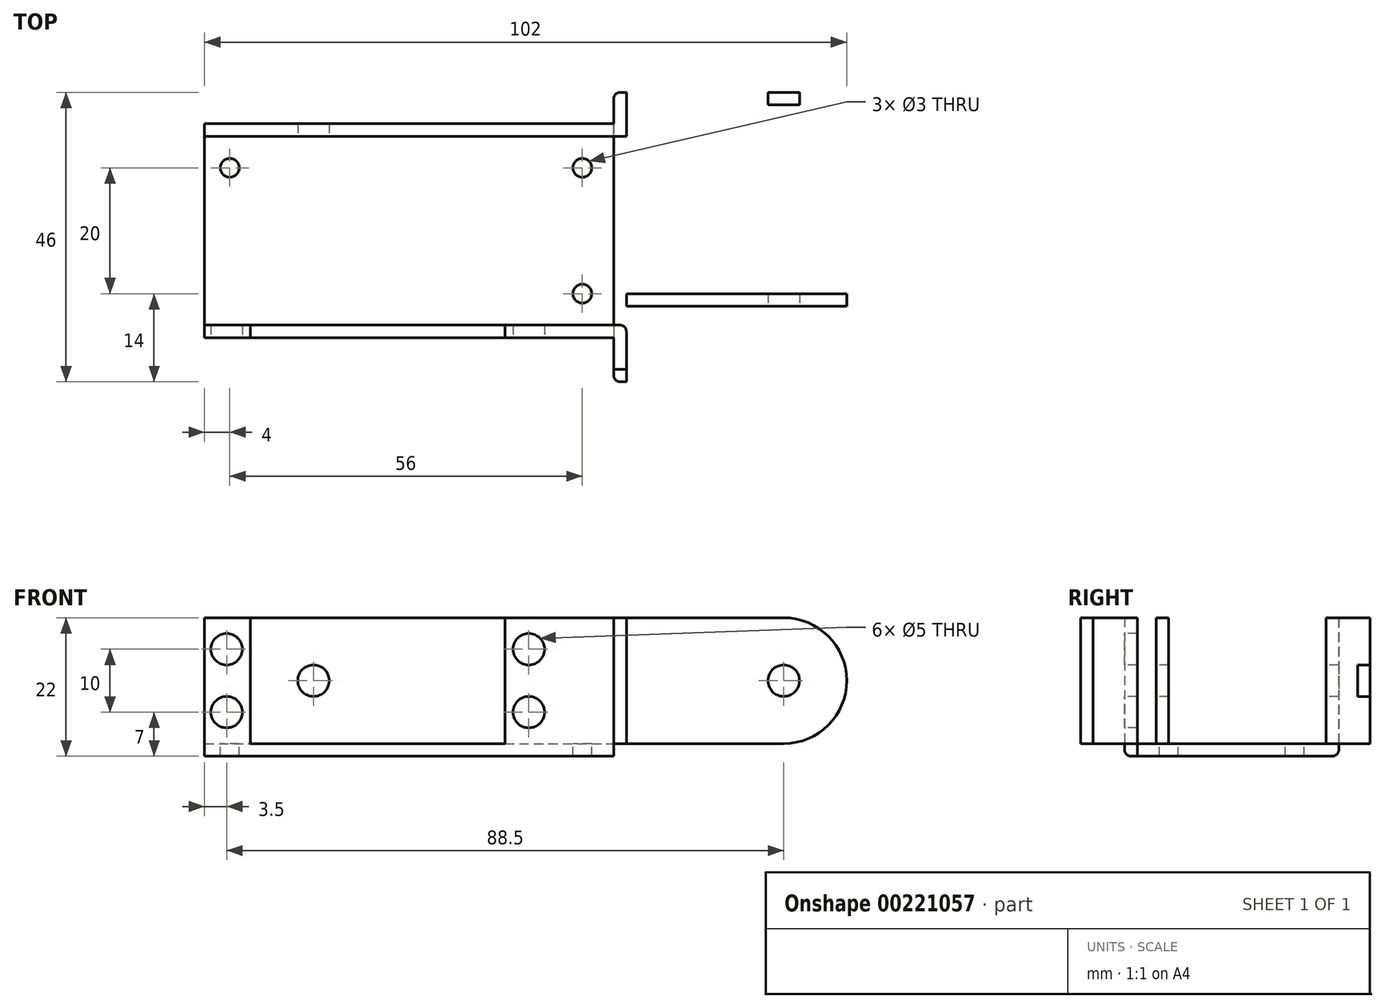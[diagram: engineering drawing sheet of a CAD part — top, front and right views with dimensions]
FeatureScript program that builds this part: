
annotation { "Feature Type Name" : "Feature", "Feature Type Description" : "" }
export const myFeature = defineFeature(function(context is Context, id is Id, definition is map)
    precondition{}
    {
        {
            var Q0;
            Q0=qCreatedBy(makeId("Front.planeOp"),FACE);
            var sketch = newSketch(context, id + "F0", { "sketchPlane" : qUnion([Q0])});
            skLineSegment(sketch, "E0.bottom", {"start": v(-27.5, 10) * mm, "end": v(-20.2, 10) * mm});
            skLineSegment(sketch, "E0.top", {"start": v(-27.5, -10) * mm, "end": v(27.5, -10) * mm});
            skLineSegment(sketch, "E0.left", {"start": v(-27.5, 10) * mm, "end": v(-27.5, -10) * mm});
            skLineSegment(sketch, "E0.right", {"start": v(27.5, 10) * mm, "end": v(27.5, -10) * mm});
            skLineSegment(sketch, "E1", {"start": v(-20.2, 10) * mm, "end": v(-20.2, -10) * mm});
            skLineSegment(sketch, "E2", {"start": v(20.2, 10) * mm, "end": v(20.2, -10) * mm});
            skCircle(sketch, "E3", {"center": v(-24, 5) * mm, "radius": 2.5 * mm});
            skCircle(sketch, "E4", {"center": v(-24, -5) * mm, "radius": 2.5 * mm});
            skCircle(sketch, "E5", {"center": v(24, 5) * mm, "radius": 2.5 * mm});
            skCircle(sketch, "E6", {"center": v(24, -5) * mm, "radius": 2.5 * mm});
            skLineSegment(sketch, "E7", {"start": v(-27.5, -10) * mm, "end": v(-27.5, -12) * mm});
            skLineSegment(sketch, "E8", {"start": v(-27.5, -12) * mm, "end": v(27.5, -12) * mm});
            skLineSegment(sketch, "E9", {"start": v(27.5, -12) * mm, "end": v(27.5, -10) * mm});
            skLineSegment(sketch, "E10.trimOffspring", {"start": v(20.2, 10) * mm, "end": v(27.5, 10) * mm});
            skLineSegment(sketch, "E11", {"start": v(37.5, 10) * mm, "end": v(37.5, -12) * mm});
            skLineSegment(sketch, "E12", {"start": v(37.5, -12) * mm, "end": v(27.5, -12) * mm});
            skLineSegment(sketch, "E13", {"start": v(37.5, 10) * mm, "end": v(39.5, 10) * mm});
            skLineSegment(sketch, "E14", {"start": v(39.5, 10) * mm, "end": v(39.5, -10) * mm});
            skLineSegment(sketch, "E15", {"start": v(27.5, 10) * mm, "end": v(37.5, 10) * mm});
            skLineSegment(sketch, "E16", {"start": v(39.5, -10) * mm, "end": v(37.5, -10) * mm});
            skCircle(sketch, "E17", {"center": v(64.5, 0) * mm, "radius": 2.5 * mm});
            skArc(sketch, "E18", {"start": v(64.5, -10) * mm, "mid": v(74.5, 0) * mm, "end": v(64.5, 10) * mm});
            skLineSegment(sketch, "E19", {"start": v(64.5, 10) * mm, "end": v(39.5, 10) * mm});
            skLineSegment(sketch, "E20", {"start": v(64.5, -10) * mm, "end": v(39.5, -10) * mm});
            skLineSegment(sketch, "E21", {"start": v(27.5, -10) * mm, "end": v(37.5, -10) * mm});
            skSolve(sketch);
        }
        {
            var Q0;
            Q0=qCreatedBy(makeId("Top.planeOp"),FACE);
            var sketch = newSketch(context, id + "F1", { "sketchPlane" : qUnion([Q0])});
            skLineSegment(sketch, "E22", {"start": v(-27.5, 34) * mm, "end": v(-27.5, 2) * mm});
            skLineSegment(sketch, "E23", {"start": v(-27.5, 2) * mm, "end": v(37.5, 2) * mm});
            skLineSegment(sketch, "E24", {"start": v(-27.5, 32) * mm, "end": v(37.5, 32) * mm});
            skLineSegment(sketch, "E25", {"start": v(-27.5, 2) * mm, "end": v(-27.5, 0) * mm});
            skLineSegment(sketch, "E26", {"start": v(-27.5, 0) * mm, "end": v(27.5, 0) * mm});
            skLineSegment(sketch, "E27", {"start": v(-27.5, 34) * mm, "end": v(37.44, 34) * mm});
            skLineSegment(sketch, "E28", {"start": v(37.44, 34) * mm, "end": v(37.44, 32) * mm});
            skLineSegment(sketch, "E29", {"start": v(27.5, 0) * mm, "end": v(37.5, 0) * mm});
            skLineSegment(sketch, "E30", {"start": v(37.5, 0) * mm, "end": v(37.5, 32) * mm});
            skCircle(sketch, "E31", {"center": v(32.5, 7) * mm, "radius": 1.5 * mm});
            skCircle(sketch, "E32", {"center": v(32.5, 27) * mm, "radius": 1.5 * mm});
            skCircle(sketch, "E33", {"center": v(-23.5, 27) * mm, "radius": 1.5 * mm});
            skSolve(sketch);
        }
        {
            var Q0;
            {var subQ0=sQuery(id+"F0.wireOp",EDGE,"E13");Q0=makeQuery(id+"F0.imprint","IMPRINT",FACE,{"disambiguationData":[TD([[makeQuery(id+"F0.imprint","IMPRINT",EDGE,{"derivedFrom":subQ0}),-1.0]])]});}
            var Q1;
            Q1=makeQuery(id+"F0.imprint","IMPRINT",FACE,{"disambiguationData":[TD([[makeQuery(id+"F0.imprint","IMPRINT",EDGE,{"derivedFrom":sQuery(id+"F0.wireOp",EDGE,"E0.right")}),1.0]])]});
            var Q2;
            {var subQ0=sQuery(id+"F0.wireOp",EDGE,"E0.right");Q2=makeQuery(id+"F0.imprint","IMPRINT",FACE,{"disambiguationData":[TD([[makeQuery(id+"F0.imprint","IMPRINT",EDGE,{"derivedFrom":subQ0}),-1.0]])]});}
            var Q3;
            Q3=makeQuery(id+"F0.imprint","IMPRINT",FACE,{"disambiguationData":[TD([[makeQuery(id+"F0.imprint","IMPRINT",EDGE,{"derivedFrom":sQuery(id+"F0.wireOp",EDGE,"E9")}),-1.0]])]});
            var Q4;
            {var subQ0=sQuery(id+"F0.wireOp",EDGE,"E7");Q4=makeQuery(id+"F0.imprint","IMPRINT",FACE,{"disambiguationData":[TD([[makeQuery(id+"F0.imprint","IMPRINT",EDGE,{"derivedFrom":subQ0}),1.0]])]});}
            var Q5;
            Q5=makeQuery(id+"F0.imprint","IMPRINT",FACE,{"disambiguationData":[TD([[makeQuery(id+"F0.imprint","IMPRINT",EDGE,{"derivedFrom":sQuery(id+"F0.wireOp",EDGE,"E0.bottom")}),-1.0]])]});
            extrude(context, id + "F2", {"entities" : qUnion([Q0, Q1, Q2, Q3, Q4, Q5]), "oppositeDirection" : true, "depth" : 2 * mm});
        }
        {
            var Q0;
            {var subQ4=sQuery(id+"F1.wireOp",EDGE,"E23");Q0=makeQuery(id+"F1.imprint","IMPRINT",FACE,{"disambiguationData":[TD([[makeQuery(id+"F1.imprint","IMPRINT",EDGE,{"derivedFrom":subQ4}),1.0]])]});}
            extrude(context, id + "F3", {"entities" : qUnion([Q0]), "oppositeDirection" : true, "depth" : 2 * mm});
        }
        {
            var Q0;
            Q0=makeQuery(id+"F3.opExtrude","SWEPT_BODY",BODY,{"disambiguationData":[OSD([sQuery(id+"F1.wireOp",EDGE,"E22"),sQuery(id+"F1.wireOp",EDGE,"E23"),sQuery(id+"F1.wireOp",EDGE,"E24"),sQuery(id+"F1.wireOp",EDGE,"E27"),sQuery(id+"F1.wireOp",EDGE,"E28"),sQuery(id+"F1.wireOp",EDGE,"E30")])]});
            var Q1;
            Q1=makeQuery(id+"F2.opExtrude","CAP_EDGE",EDGE,{"disambiguationData":[OSD([sQuery(id+"F0.wireOp",EDGE,"E0.left"),sQuery(id+"F0.wireOp",EDGE,"E7")])],"isStart":false});
            transform(context, id + "F4", {"entities" : qUnion([Q0]), "transformType" : TransformType.TRANSLATION_DISTANCE, "transformDirection" : qUnion([Q1]), "distance" : 10 * mm, "makeCopy" : false});
        }
        {
            var Q0;
            {var subQ0=sQuery(id+"F0.wireOp",EDGE,"E13");Q0=makeQuery(id+"F0.imprint","IMPRINT",FACE,{"disambiguationData":[TD([[makeQuery(id+"F0.imprint","IMPRINT",EDGE,{"derivedFrom":subQ0}),-1.0]])]});}
            extrude(context, id + "F5", {"entities" : qUnion([Q0]), "operationType" : NewBodyOperationType.ADD, "depth" : 5 * mm});
        }
        {
            var Q0;
            Q0=makeQuery(id+"F0.imprint","IMPRINT",FACE,{"disambiguationData":[TD([[makeQuery(id+"F0.imprint","IMPRINT",EDGE,{"derivedFrom":sQuery(id+"F0.wireOp",EDGE,"E14")}),1.0]])]});
            var Q1;
            Q1=makeQuery(id+"F5.opExtrude","CAP_FACE",FACE,{"disambiguationData":[OSD([sQuery(id+"F0.wireOp",EDGE,"E11"),sQuery(id+"F0.wireOp",EDGE,"E13"),sQuery(id+"F0.wireOp",EDGE,"E14"),sQuery(id+"F0.wireOp",EDGE,"E16")])],"isStart":false});
            extrude(context, id + "F6", {"entities" : qUnion([Q0, Q1]), "depth" : 2 * mm});
        }
        {
            var Q0;
            Q0=makeQuery(id+"F6.opExtrude","SWEPT_BODY",BODY,{"disambiguationData":[OSD([sQuery(id+"F0.wireOp",EDGE,"E14"),sQuery(id+"F0.wireOp",EDGE,"E17"),sQuery(id+"F0.wireOp",EDGE,"E18"),sQuery(id+"F0.wireOp",EDGE,"E19"),sQuery(id+"F0.wireOp",EDGE,"E20")])]});
            var Q1;
            {var subQ0=sQuery(id+"F0.wireOp",EDGE,"E19");var subQ1=sQuery(id+"F0.wireOp",EDGE,"E14");var subQ2=sQuery(id+"F0.wireOp",EDGE,"E13");Q1=makeQuery(id+"F5.boolean.opBoolean","MERGE",EDGE,{"derivedFrom":[makeQuery(id+"F2.opExtrude","SWEPT_EDGE",EDGE,{"disambiguationData":[OSD([subQ2,subQ1,subQ0])]}),makeQuery(id+"F5.opExtrude","SWEPT_EDGE",EDGE,{"disambiguationData":[OSD([subQ2,subQ1,subQ0])]})]});}
            var Q2;
            {var subQ0=sQuery(id+"F0.wireOp",EDGE,"E19");var subQ1=sQuery(id+"F0.wireOp",EDGE,"E14");var subQ2=sQuery(id+"F0.wireOp",EDGE,"E13");Q2=makeQuery(id+"F5.boolean.opBoolean","MERGE",EDGE,{"derivedFrom":[makeQuery(id+"F2.opExtrude","SWEPT_EDGE",EDGE,{"disambiguationData":[OSD([subQ2,subQ1,subQ0])]}),makeQuery(id+"F5.opExtrude","SWEPT_EDGE",EDGE,{"disambiguationData":[OSD([subQ2,subQ1,subQ0])]})]});}
            transform(context, id + "F7", {"entities" : qUnion([Q0]), "transformType" : TransformType.TRANSLATION_DISTANCE, "transformDirection" : qUnion([Q2]), "distance" : 5 * mm, "makeCopy" : false});
        }
        {
            var Q0;
            Q0=makeQuery(id+"F3.opExtrude","SWEPT_FACE",FACE,{"disambiguationData":[OSD([sQuery(id+"F1.wireOp",EDGE,"E24")])]});
            var sketch = newSketch(context, id + "F8", { "sketchPlane" : qUnion([Q0])});
            skCircle(sketch, "E34.MirrorC", {"center": v(-64.5, 0) * mm, "radius": 2.5 * mm});
            skLineSegment(sketch, "E35.MirrorCS", {"start": v(27.5, 10) * mm, "end": v(27.5, -10) * mm});
            skCircle(sketch, "E36", {"center": v(10.2, 0) * mm, "radius": 2.5 * mm});
            skLineSegment(sketch, "E37", {"start": v(-37.5, -10) * mm, "end": v(-37.5, 10) * mm});
            skLineSegment(sketch, "E38", {"start": v(-37.5, 10) * mm, "end": v(-39.5, 10) * mm});
            skLineSegment(sketch, "E39", {"start": v(-39.5, 10) * mm, "end": v(-39.5, -10) * mm});
            skLineSegment(sketch, "E40", {"start": v(-39.5, -10) * mm, "end": v(-37.5, -10) * mm});
            skLineSegment(sketch, "E41", {"start": v(-37.5, -10) * mm, "end": v(-37.5, -12) * mm});
            skLineSegment(sketch, "E42", {"start": v(-37.5, 10) * mm, "end": v(27.5, 10) * mm});
            skLineSegment(sketch, "E43", {"start": v(-39.5, 10) * mm, "end": v(-64.5, 10) * mm});
            skLineSegment(sketch, "E44", {"start": v(-39.5, -10) * mm, "end": v(-64.5, -10) * mm});
            skArc(sketch, "E45", {"start": v(-64.5, 10) * mm, "mid": v(-74.5, 0) * mm, "end": v(-64.5, -10) * mm});
            skSolve(sketch);
        }
        {
            var Q0;
            Q0=makeQuery(id+"F8.imprint","IMPRINT",FACE,{"disambiguationData":[TD([[makeQuery(id+"F8.imprint","IMPRINT",EDGE,{"derivedFrom":sQuery(id+"F8.wireOp",EDGE,"E35.MirrorCS")}),-1.0]])]});
            var Q1;
            Q1=makeQuery(id+"F8.imprint","IMPRINT",FACE,{"disambiguationData":[TD([[makeQuery(id+"F8.imprint","IMPRINT",EDGE,{"derivedFrom":sQuery(id+"F8.wireOp",EDGE,"E41")}),-1.0]])]});
            extrude(context, id + "F9", {"entities" : qUnion([Q0, Q1]), "depth" : 2 * mm});
        }
        {
            var Q0;
            Q0=makeQuery(id+"F8.imprint","IMPRINT",FACE,{"disambiguationData":[TD([[makeQuery(id+"F8.imprint","IMPRINT",EDGE,{"derivedFrom":sQuery(id+"F8.wireOp",EDGE,"E37")}),1.0]])]});
            extrude(context, id + "F10", {"entities" : qUnion([Q0]), "operationType" : NewBodyOperationType.ADD, "depth" : 7 * mm});
        }
        {
            var Q0;
            Q0=makeQuery(id+"F8.imprint","IMPRINT",FACE,{"disambiguationData":[TD([[makeQuery(id+"F8.imprint","IMPRINT",EDGE,{"derivedFrom":sQuery(id+"F8.wireOp",EDGE,"E34.MirrorC")}),1.0]])]});
            extrude(context, id + "F11", {"entities" : qUnion([Q0]), "depth" : 2 * mm});
        }
        {
            var Q0;
            Q0=makeQuery(id+"F11.opExtrude","SWEPT_BODY",BODY,{"disambiguationData":[OSD([sQuery(id+"F8.wireOp",EDGE,"E34.MirrorC"),sQuery(id+"F8.wireOp",EDGE,"E39"),sQuery(id+"F8.wireOp",EDGE,"E43"),sQuery(id+"F8.wireOp",EDGE,"E44"),sQuery(id+"F8.wireOp",EDGE,"xCFFjOfr-ZHEl-xtIQ-mPX2-yJkaWQiFbmXC")])]});
            var Q1;
            Q1=makeQuery(id+"F10.opExtrude","SWEPT_EDGE",EDGE,{"disambiguationData":[OSD([sQuery(id+"F8.wireOp",EDGE,"E38"),sQuery(id+"F8.wireOp",EDGE,"E39"),sQuery(id+"F8.wireOp",EDGE,"E43")])]});
            transform(context, id + "F12", {"entities" : qUnion([Q0]), "transformType" : TransformType.TRANSLATION_DISTANCE, "transformDirection" : qUnion([Q1]), "distance" : 5 * mm, "oppositeDirection" : true, "makeCopy" : false});
        }
        {
            var Q0;
            Q0=makeQuery(id+"F9.opExtrude","CAP_EDGE",EDGE,{"disambiguationData":[OSD([sQuery(id+"F1.wireOp",EDGE,"E24")])],"isStart":false});
            fillet(context, id + "F13", {"entities" : qUnion([Q0]), "radius" : 1 * mm, "tangentPropagation" : true, "allowEdgeOverflow" : false});
        }
        {
            var Q0;
            Q0=makeQuery(id+"F2.opExtrude","CAP_EDGE",EDGE,{"disambiguationData":[OSD([sQuery(id+"F0.wireOp",EDGE,"E8"),sQuery(id+"F0.wireOp",EDGE,"E12")])],"isStart":true});
            fillet(context, id + "F14", {"entities" : qUnion([Q0]), "radius" : 1 * mm, "tangentPropagation" : true, "allowEdgeOverflow" : false});
        }
        {
            var Q0;
            Q0=makeQuery(id+"F2.opExtrude","CAP_EDGE",EDGE,{"disambiguationData":[OSD([sQuery(id+"F0.wireOp",EDGE,"E14")])],"isStart":false});
            fillet(context, id + "F15", {"entities" : qUnion([Q0]), "radius" : 1 * mm, "tangentPropagation" : true, "allowEdgeOverflow" : false});
        }
        {
            var Q0;
            Q0=makeQuery(id+"F10.opExtrude","CAP_EDGE",EDGE,{"disambiguationData":[OSD([sQuery(id+"F8.wireOp",EDGE,"E37")])],"isStart":false});
            fillet(context, id + "F16", {"entities" : qUnion([Q0]), "radius" : 1 * mm, "tangentPropagation" : true, "allowEdgeOverflow" : false});
        }
        {
            var Q0;
            Q0=makeQuery(id+"F6.opExtrude","CAP_EDGE",EDGE,{"disambiguationData":[OSD([sQuery(id+"F0.wireOp",EDGE,"E11")])],"isStart":false});
            fillet(context, id + "F17", {"entities" : qUnion([Q0]), "radius" : 1 * mm, "tangentPropagation" : true, "allowEdgeOverflow" : false});
        }
        {
            var Q0;
            Q0=makeQuery(id+"F6.opExtrude","SWEPT_BODY",BODY,{"disambiguationData":[OSD([sQuery(id+"F0.wireOp",EDGE,"E14"),sQuery(id+"F0.wireOp",EDGE,"E17"),sQuery(id+"F0.wireOp",EDGE,"E18"),sQuery(id+"F0.wireOp",EDGE,"E19"),sQuery(id+"F0.wireOp",EDGE,"E20")])]});
            var Q1;
            Q1=qCreatedBy(makeId("Front.planeOp"),FACE);
            mirror(context, id + "F18", {"entities" : qUnion([Q0]), "mirrorPlane" : qUnion([Q1])});
        }
        {
            var Q0;
            Q0=makeQuery(id+"F6.opExtrude","SWEPT_BODY",BODY,{"disambiguationData":[OSD([sQuery(id+"F0.wireOp",EDGE,"E14"),sQuery(id+"F0.wireOp",EDGE,"E17"),sQuery(id+"F0.wireOp",EDGE,"E18"),sQuery(id+"F0.wireOp",EDGE,"E19"),sQuery(id+"F0.wireOp",EDGE,"E20")])]});
            deleteBodies(context, id + "F19", {"entities" : qUnion([Q0])});
        }
    });
